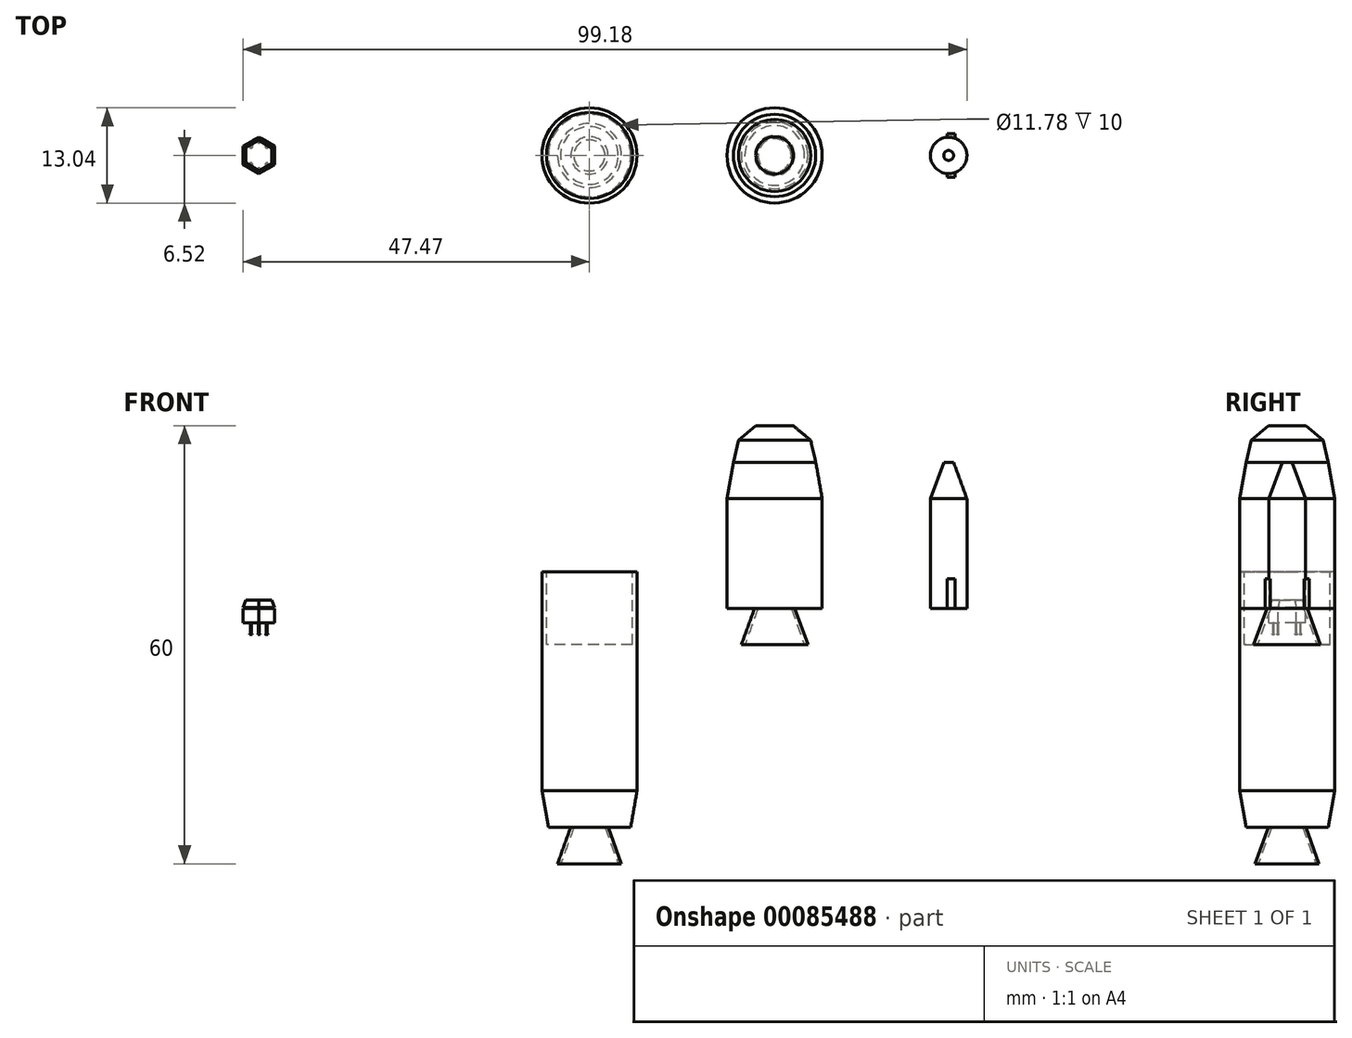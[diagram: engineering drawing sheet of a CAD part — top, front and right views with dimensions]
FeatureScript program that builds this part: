
annotation { "Feature Type Name" : "Feature", "Feature Type Description" : "" }
export const myFeature = defineFeature(function(context is Context, id is Id, definition is map)
    precondition{}
    {
        {
            var Q0;
            Q0=qCreatedBy(makeId("Top.planeOp"),FACE);
            var sketch = newSketch(context, id + "F0", { "sketchPlane" : qUnion([Q0])});
            skCircle(sketch, "E0", {"center": v(0, 0) * mm, "radius": 6.52 * mm});
            skSolve(sketch);
        }
        {
            var Q0;
            Q0=makeQuery(id+"F0.imprint","IMPRINT",FACE,{"disambiguationData":[TD([[makeQuery(id+"F0.imprint","IMPRINT",EDGE,{"derivedFrom":sQuery(id+"F0.wireOp",EDGE,"E0")}),1.0]])]});
            extrude(context, id + "F1", {"entities" : qUnion([Q0]), "depth" : 5 * mm, "hasSecondDirection" : true, "secondDirectionOppositeDirection" : true, "secondDirectionDepth" : 25 * mm});
        }
        {
            var Q0;
            Q0=makeQuery(id+"F1.opExtrude","CAP_FACE",FACE,{"disambiguationData":[OSD([sQuery(id+"F0.wireOp",EDGE,"E0")])],"isStart":true});
            extrude(context, id + "F2", {"entities" : qUnion([Q0]), "operationType" : NewBodyOperationType.ADD, "depth" : 5 * mm, "hasDraft" : true, "draftAngle" : 10 * degree, "draftPullDirection" : true});
        }
        {
            var Q0;
            Q0=makeQuery(id+"F2.opExtrude","CAP_FACE",FACE,{"disambiguationData":[OSD([sQuery(id+"F0.wireOp",EDGE,"E0")])],"isStart":false});
            var sketch = newSketch(context, id + "F3", { "sketchPlane" : qUnion([Q0])});
            skCircle(sketch, "E1", {"center": v(0, 0) * mm, "radius": 2.56 * mm});
            skSolve(sketch);
        }
        {
            var Q0;
            Q0 = qSketchRegion(id + "F3", true);
            extrude(context, id + "F4", {"entities" : qUnion([Q0]), "operationType" : NewBodyOperationType.ADD, "depth" : 5 * mm, "hasDraft" : true, "draftAngle" : 20 * degree});
        }
        {
            var Q0;
            Q0=makeQuery(id+"F4.opExtrude","CAP_FACE",FACE,{"disambiguationData":[OSD([sQuery(id+"F3.wireOp",EDGE,"E1")])],"isStart":false});
            var sketch = newSketch(context, id + "F5", { "sketchPlane" : qUnion([Q0])});
            skCircle(sketch, "E2", {"center": v(0, 0) * mm, "radius": 3.95 * mm});
            skSolve(sketch);
        }
        {
            var Q0;
            Q0 = qSketchRegion(id + "F5", true);
            extrude(context, id + "F6", {"entities" : qUnion([Q0]), "operationType" : NewBodyOperationType.REMOVE, "oppositeDirection" : true, "depth" : 5 * mm, "hasDraft" : true, "draftAngle" : 20 * degree, "draftPullDirection" : true});
        }
        {
            var Q0;
            Q0=makeQuery(id+"F1.opExtrude","CAP_FACE",FACE,{"disambiguationData":[OSD([sQuery(id+"F0.wireOp",EDGE,"E0")])],"isStart":false});
            var sketch = newSketch(context, id + "F7", { "sketchPlane" : qUnion([Q0])});
            skCircle(sketch, "E3", {"center": v(0, 0) * mm, "radius": 5.9 * mm});
            skSolve(sketch);
        }
        {
            var Q0;
            Q0 = qSketchRegion(id + "F7", true);
            extrude(context, id + "F8", {"entities" : qUnion([Q0]), "operationType" : NewBodyOperationType.REMOVE, "oppositeDirection" : true, "depth" : 10 * mm});
        }
        {
            var Q0;
            Q0=qCreatedBy(makeId("Top.planeOp"),FACE);
            var sketch = newSketch(context, id + "F9", { "sketchPlane" : qUnion([Q0])});
            skCircle(sketch, "E4", {"center": v(25.36, 0) * mm, "radius": 6.52 * mm});
            skSolve(sketch);
        }
        {
            var Q0;
            Q0=makeQuery(id+"F9.imprint","IMPRINT",FACE,{"disambiguationData":[TD([[makeQuery(id+"F9.imprint","IMPRINT",EDGE,{"derivedFrom":sQuery(id+"F9.wireOp",EDGE,"E4")}),1.0]])]});
            extrude(context, id + "F10", {"entities" : qUnion([Q0]), "depth" : 15 * mm});
        }
        {
            var Q0;
            Q0=makeQuery(id+"F10.opExtrude","CAP_FACE",FACE,{"disambiguationData":[OSD([sQuery(id+"F9.wireOp",EDGE,"E4")])],"isStart":true});
            var sketch = newSketch(context, id + "F11", { "sketchPlane" : qUnion([Q0])});
            skCircle(sketch, "E5", {"center": v(25.36, 0) * mm, "radius": 2.74 * mm});
            skSolve(sketch);
        }
        {
            var Q0;
            Q0 = qSketchRegion(id + "F11", true);
            extrude(context, id + "F12", {"entities" : qUnion([Q0]), "operationType" : NewBodyOperationType.ADD, "depth" : 5 * mm, "hasDraft" : true, "draftAngle" : 20 * degree});
        }
        {
            var Q0;
            Q0=makeQuery(id+"F12.opExtrude","CAP_FACE",FACE,{"disambiguationData":[OSD([sQuery(id+"F11.wireOp",EDGE,"E5")])],"isStart":false});
            var sketch = newSketch(context, id + "F13", { "sketchPlane" : qUnion([Q0])});
            skCircle(sketch, "E6", {"center": v(25.36, 0) * mm, "radius": 4.1 * mm});
            skSolve(sketch);
        }
        {
            var Q0;
            Q0 = qSketchRegion(id + "F13", true);
            extrude(context, id + "F14", {"entities" : qUnion([Q0]), "operationType" : NewBodyOperationType.REMOVE, "oppositeDirection" : true, "depth" : 5 * mm, "hasDraft" : true, "draftAngle" : 20 * degree, "draftPullDirection" : true});
        }
        {
            var Q0;
            Q0=makeQuery(id+"F10.opExtrude","CAP_FACE",FACE,{"disambiguationData":[OSD([sQuery(id+"F9.wireOp",EDGE,"E4")])],"isStart":false});
            extrude(context, id + "F15", {"entities" : qUnion([Q0]), "operationType" : NewBodyOperationType.ADD, "depth" : 5 * mm, "hasDraft" : true, "draftAngle" : 10 * degree, "draftPullDirection" : true});
        }
        {
            var Q0;
            Q0=makeQuery(id+"F15.opExtrude","CAP_FACE",FACE,{"disambiguationData":[OSD([sQuery(id+"F9.wireOp",EDGE,"E4")])],"isStart":false});
            extrude(context, id + "F16", {"entities" : qUnion([Q0]), "operationType" : NewBodyOperationType.ADD, "depth" : 3 * mm, "hasDraft" : true, "draftAngle" : 13 * degree, "draftPullDirection" : true});
        }
        {
            var Q0;
            Q0=makeQuery(id+"F16.opExtrude","CAP_FACE",FACE,{"disambiguationData":[OSD([sQuery(id+"F9.wireOp",EDGE,"E4")])],"isStart":false});
            extrude(context, id + "F17", {"entities" : qUnion([Q0]), "operationType" : NewBodyOperationType.ADD, "depth" : 2 * mm, "hasDraft" : true, "draftAngle" : 50 * degree, "draftPullDirection" : true});
        }
        {
            var Q0;
            Q0=qCreatedBy(makeId("Top.planeOp"),FACE);
            var sketch = newSketch(context, id + "F18", { "sketchPlane" : qUnion([Q0])});
            skCircle(sketch, "E7", {"center": v(49.21, 0) * mm, "radius": 2.5 * mm});
            skSolve(sketch);
        }
        {
            var Q0;
            Q0 = qSketchRegion(id + "F18", true);
            extrude(context, id + "F19", {"entities" : qUnion([Q0]), "depth" : 15 * mm});
        }
        {
            var Q0;
            Q0=makeQuery(id+"F19.opExtrude","CAP_FACE",FACE,{"disambiguationData":[OSD([sQuery(id+"F18.wireOp",EDGE,"E7")])],"isStart":false});
            extrude(context, id + "F20", {"entities" : qUnion([Q0]), "operationType" : NewBodyOperationType.ADD, "depth" : 5 * mm, "hasDraft" : true, "draftAngle" : 20 * degree, "draftPullDirection" : true});
        }
        {
            var Q0;
            Q0=qCreatedBy(makeId("Front.planeOp"),FACE);
            var sketch = newSketch(context, id + "F21", { "sketchPlane" : qUnion([Q0])});
            skLineSegment(sketch, "E8.bottom", {"start": v(50.08, 4.04) * mm, "end": v(49, 4.04) * mm});
            skLineSegment(sketch, "E8.top", {"start": v(50.08, 0) * mm, "end": v(49, 0) * mm});
            skLineSegment(sketch, "E8.left", {"start": v(50.08, 4.04) * mm, "end": v(50.08, 0) * mm});
            skLineSegment(sketch, "E8.right", {"start": v(49, 4.04) * mm, "end": v(49, 0) * mm});
            skSolve(sketch);
        }
        {
            var Q0;
            Q0 = qSketchRegion(id + "F21", true);
            extrude(context, id + "F22", {"entities" : qUnion([Q0]), "operationType" : NewBodyOperationType.ADD, "depth" : 3 * mm, "hasSecondDirection" : true, "secondDirectionOppositeDirection" : true, "secondDirectionDepth" : 3 * mm});
        }
        {
            var Q0;
            Q0=qCreatedBy(makeId("Top.planeOp"),FACE);
            var sketch = newSketch(context, id + "F23", { "sketchPlane" : qUnion([Q0])});
            skCircle(sketch, "E9.cCircle", {"center": v(-45.28, 0) * mm, "radius": 2.16 * mm, "construction": true});
            skLineSegment(sketch, "E9.0", {"start": v(-43.12, 1.25) * mm, "end": v(-43.12, -1.25) * mm});
            skLineSegment(sketch, "E9.1", {"start": v(-43.12, -1.25) * mm, "end": v(-45.28, -2.5) * mm});
            skLineSegment(sketch, "E9.2", {"start": v(-45.28, -2.5) * mm, "end": v(-47.45, -1.25) * mm});
            skLineSegment(sketch, "E9.3", {"start": v(-47.45, -1.25) * mm, "end": v(-47.45, 1.25) * mm});
            skLineSegment(sketch, "E9.4", {"start": v(-47.45, 1.25) * mm, "end": v(-45.28, 2.5) * mm});
            skLineSegment(sketch, "E9.5", {"start": v(-45.28, 2.5) * mm, "end": v(-43.12, 1.25) * mm});
            skPoint(sketch, "E9.0.midPoint", {"position": v(-43.12, 0) * mm});
            skSolve(sketch);
        }
        {
            var Q0;
            Q0=makeQuery(id+"F23.imprint","IMPRINT",FACE,{"disambiguationData":[TD([[makeQuery(id+"F23.imprint","IMPRINT",EDGE,{"derivedFrom":sQuery(id+"F23.wireOp",EDGE,"E9.0")}),-1.0]])]});
            extrude(context, id + "F24", {"entities" : qUnion([Q0]), "oppositeDirection" : true, "depth" : 2 * mm});
        }
        {
            var Q0;
            Q0=makeQuery(id+"F24.opExtrude","CAP_FACE",FACE,{"disambiguationData":[OSD([sQuery(id+"F23.wireOp",EDGE,"E9.0"),sQuery(id+"F23.wireOp",EDGE,"E9.1"),sQuery(id+"F23.wireOp",EDGE,"E9.2"),sQuery(id+"F23.wireOp",EDGE,"E9.3"),sQuery(id+"F23.wireOp",EDGE,"E9.4"),sQuery(id+"F23.wireOp",EDGE,"E9.5")])],"isStart":true});
            var sketch = newSketch(context, id + "F25", { "sketchPlane" : qUnion([Q0])});
            skCircle(sketch, "E10", {"center": v(-45.28, -1.87) * mm, "radius": 0.17 * mm});
            skPoint(sketch, "E10.centerSnap0", {"position": v(-46.37, -1.87) * mm});
            skCircle(sketch, "E11", {"center": v(-44.2, -1.25) * mm, "radius": 0.22 * mm});
            skPoint(sketch, "E11.centerSnap0", {"position": v(-44.2, -1.87) * mm});
            skCircle(sketch, "E12", {"center": v(-44.2, 1.25) * mm, "radius": 0.23 * mm});
            skPoint(sketch, "E12.centerSnap0", {"position": v(-44.2, 1.87) * mm});
            skCircle(sketch, "E13", {"center": v(-46.37, 1.25) * mm, "radius": 0.24 * mm});
            skPoint(sketch, "E13.centerSnap0", {"position": v(-46.37, 1.87) * mm});
            skCircle(sketch, "E14", {"center": v(-46.37, -1.25) * mm, "radius": 0.23 * mm});
            skCircle(sketch, "E15", {"center": v(-45.28, 1.87) * mm, "radius": 0.18 * mm});
            skSolve(sketch);
        }
        {
            var Q0;
            Q0 = qSketchRegion(id + "F25", true);
            extrude(context, id + "F26", {"entities" : qUnion([Q0]), "operationType" : NewBodyOperationType.ADD, "depth" : 0.1 * mm});
        }
        {
            var Q0;
            Q0=makeQuery(id+"F26.opExtrude","CAP_FACE",FACE,{"disambiguationData":[OSD([sQuery(id+"F25.wireOp",EDGE,"E11")])],"isStart":false});
            var sketch = newSketch(context, id + "F27", { "sketchPlane" : qUnion([Q0])});
            skCircle(sketch, "E16.cCircle", {"center": v(-45.3, 0) * mm, "radius": 2.16 * mm, "construction": true});
            skLineSegment(sketch, "E16.0", {"start": v(-45.27, 2.5) * mm, "end": v(-43.12, 1.23) * mm});
            skLineSegment(sketch, "E16.1", {"start": v(-43.12, 1.23) * mm, "end": v(-43.15, -1.27) * mm});
            skLineSegment(sketch, "E16.2", {"start": v(-43.15, -1.27) * mm, "end": v(-45.32, -2.5) * mm});
            skLineSegment(sketch, "E16.3", {"start": v(-45.32, -2.5) * mm, "end": v(-47.47, -1.23) * mm});
            skLineSegment(sketch, "E16.4", {"start": v(-47.47, -1.23) * mm, "end": v(-47.45, 1.27) * mm});
            skLineSegment(sketch, "E16.5", {"start": v(-47.45, 1.27) * mm, "end": v(-45.27, 2.5) * mm});
            skPoint(sketch, "E16.0.midPoint", {"position": v(-44.2, 1.86) * mm});
            skSolve(sketch);
        }
        {
            var Q0;
            Q0 = qSketchRegion(id + "F27", true);
            extrude(context, id + "F28", {"entities" : qUnion([Q0]), "operationType" : NewBodyOperationType.ADD, "depth" : 1 * mm, "hasDraft" : true, "draftAngle" : 20 * degree, "draftPullDirection" : true});
        }
        {
            var Q0;
            Q0=makeQuery(id+"F24.opExtrude","CAP_FACE",FACE,{"disambiguationData":[OSD([sQuery(id+"F23.wireOp",EDGE,"E9.0"),sQuery(id+"F23.wireOp",EDGE,"E9.1"),sQuery(id+"F23.wireOp",EDGE,"E9.2"),sQuery(id+"F23.wireOp",EDGE,"E9.3"),sQuery(id+"F23.wireOp",EDGE,"E9.4"),sQuery(id+"F23.wireOp",EDGE,"E9.5")])],"isStart":false});
            var sketch = newSketch(context, id + "F29", { "sketchPlane" : qUnion([Q0])});
            skCircle(sketch, "E17", {"center": v(-45.28, 1.87) * mm, "radius": 0.06 * mm});
            skPoint(sketch, "E17.centerSnap0", {"position": v(-44.2, 1.87) * mm});
            skCircle(sketch, "E18", {"center": v(-44.2, 1.25) * mm, "radius": 0.06 * mm});
            skCircle(sketch, "E19", {"center": v(-44.2, -1.25) * mm, "radius": 0.05 * mm});
            skPoint(sketch, "E19.centerSnap0", {"position": v(-44.2, -1.87) * mm});
            skCircle(sketch, "E20", {"center": v(-45.28, -1.87) * mm, "radius": 0.04 * mm});
            skCircle(sketch, "E21", {"center": v(-46.37, -1.25) * mm, "radius": 0.05 * mm});
            skPoint(sketch, "E21.centerSnap0", {"position": v(-46.37, -1.87) * mm});
            skCircle(sketch, "E22", {"center": v(-46.37, 1.25) * mm, "radius": 0.06 * mm});
            skPoint(sketch, "E22.centerSnap0", {"position": v(-46.37, 1.87) * mm});
            skSolve(sketch);
        }
        {
            var Q0;
            Q0 = qSketchRegion(id + "F29", true);
            extrude(context, id + "F30", {"entities" : qUnion([Q0]), "operationType" : NewBodyOperationType.ADD, "depth" : 1.5 * mm});
        }
        {
            var Q0;
            Q0=makeQuery(id+"F30.opExtrude","CAP_FACE",FACE,{"disambiguationData":[OSD([sQuery(id+"F29.wireOp",EDGE,"E21")])],"isStart":false});
            var sketch = newSketch(context, id + "F31", { "sketchPlane" : qUnion([Q0])});
            skCircle(sketch, "E23", {"center": v(-46.37, -1.25) * mm, "radius": 0.17 * mm});
            skSolve(sketch);
        }
        {
            var Q0;
            Q0 = qSketchRegion(id + "F31", true);
            extrude(context, id + "F32", {"entities" : qUnion([Q0]), "operationType" : NewBodyOperationType.ADD, "depth" : 0.1 * mm});
        }
        {
            var Q0;
            Q0=makeQuery(id+"F30.opExtrude","CAP_FACE",FACE,{"disambiguationData":[OSD([sQuery(id+"F29.wireOp",EDGE,"E20")])],"isStart":false});
            var sketch = newSketch(context, id + "F33", { "sketchPlane" : qUnion([Q0])});
            skCircle(sketch, "E24", {"center": v(-45.28, -1.87) * mm, "radius": 0.15 * mm});
            skSolve(sketch);
        }
        {
            var Q0;
            Q0 = qSketchRegion(id + "F33", true);
            extrude(context, id + "F34", {"entities" : qUnion([Q0]), "operationType" : NewBodyOperationType.ADD, "depth" : 0.1 * mm});
        }
        {
            var Q0;
            Q0=makeQuery(id+"F30.opExtrude","CAP_FACE",FACE,{"disambiguationData":[OSD([sQuery(id+"F29.wireOp",EDGE,"E19")])],"isStart":false});
            var sketch = newSketch(context, id + "F35", { "sketchPlane" : qUnion([Q0])});
            skCircle(sketch, "E25", {"center": v(-44.2, -1.25) * mm, "radius": 0.16 * mm});
            skSolve(sketch);
        }
        {
            var Q0;
            Q0 = qSketchRegion(id + "F35", true);
            extrude(context, id + "F36", {"entities" : qUnion([Q0]), "operationType" : NewBodyOperationType.ADD, "depth" : 0.1 * mm});
        }
        {
            var Q0;
            Q0=makeQuery(id+"F30.opExtrude","CAP_FACE",FACE,{"disambiguationData":[OSD([sQuery(id+"F29.wireOp",EDGE,"E18")])],"isStart":false});
            var sketch = newSketch(context, id + "F37", { "sketchPlane" : qUnion([Q0])});
            skCircle(sketch, "E26", {"center": v(-44.2, 1.25) * mm, "radius": 0.14 * mm});
            skSolve(sketch);
        }
        {
            var Q0;
            Q0 = qSketchRegion(id + "F37", true);
            extrude(context, id + "F38", {"entities" : qUnion([Q0]), "operationType" : NewBodyOperationType.ADD, "depth" : 0.1 * mm});
        }
        {
            var Q0;
            Q0=makeQuery(id+"F30.opExtrude","CAP_FACE",FACE,{"disambiguationData":[OSD([sQuery(id+"F29.wireOp",EDGE,"E17")])],"isStart":false});
            var sketch = newSketch(context, id + "F39", { "sketchPlane" : qUnion([Q0])});
            skCircle(sketch, "E27", {"center": v(-45.28, 1.87) * mm, "radius": 0.17 * mm});
            skSolve(sketch);
        }
        {
            var Q0;
            Q0 = qSketchRegion(id + "F39", true);
            extrude(context, id + "F40", {"entities" : qUnion([Q0]), "operationType" : NewBodyOperationType.ADD, "depth" : 0.1 * mm});
        }
        {
            var Q0;
            Q0=makeQuery(id+"F30.opExtrude","CAP_FACE",FACE,{"disambiguationData":[OSD([sQuery(id+"F29.wireOp",EDGE,"E22")])],"isStart":false});
            var sketch = newSketch(context, id + "F41", { "sketchPlane" : qUnion([Q0])});
            skCircle(sketch, "E28", {"center": v(-46.37, 1.25) * mm, "radius": 0.18 * mm});
            skSolve(sketch);
        }
        {
            var Q0;
            Q0 = qSketchRegion(id + "F41", true);
            extrude(context, id + "F42", {"entities" : qUnion([Q0]), "operationType" : NewBodyOperationType.ADD, "depth" : 0.1 * mm});
        }
    });
